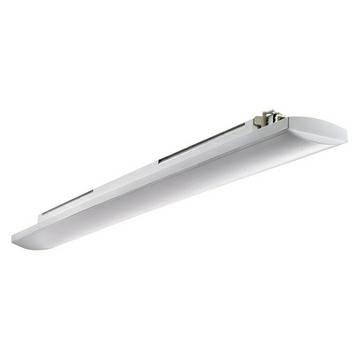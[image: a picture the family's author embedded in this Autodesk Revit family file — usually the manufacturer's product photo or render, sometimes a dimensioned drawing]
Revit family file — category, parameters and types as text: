
# Revit family: Lighting-Industriale-GEWISS-SMART[3]-PLAFONIERA-LED_OPALE_1200mm
name_source: partatom
category: Apparecchi per illuminazione
units: mm (PartAtom-declared; Revit-internal decimal feet)

## family parameters
Condiviso = No
Host = Superficie
Numero OmniClass = 23.80.70.11
Punto di calcolo locali = Sì
Quota connettore circolare = Usa diametro
Sorgente d'illuminazione = No
Taglio con vuoti quando caricato = No
Tipo di parte = Normale
Titolo OmniClass = Luminaries for Internal Lighting

## types (1)
- Lighting-Industriale-GEWISS-SMART[3]-PLAFONIERA-LED_OPALE_1200mm
    Apparecchio a ridotta temperatura superficiale = Conforme
    Applicazione = Interno
    Carico apparente = 45 VA
    Catalogo = LIGHTING
    Catalogo Serie = SMART [3]
    Classe di efficienza LED integrati = A ÷ A++
    Classe isolamento = II
    Codice EAN = 8011564877061
    Codice Electrocod = 2434
    Commenti sul wattaggio = 45W
    Descrizione = SMART3 1200 63LED 45W OPALE DALI 3000K
    Failure rate apparecchio (35.000h, Tq=35° C) = <2,5%
    Failure rate apparecchio (50.000h, Tq=25° C) = <2,5%
    Flusso nominale (lm) = 5500
    Ganci = GEWISS  - ALLUMINIO
    Garanzia = 5 anni
    Glow Wire Test = 850°C
    Grado di protezione = IP66/IP69
    IDF = 88a93abf-ed4e-4284-b5e5-3f2e7fa50ef6
    IDT = 6d1ae202-d28e-42ab-a03c-f890c181dcac
    Immagine tipo = GWS3136P.jpg
    LED Life time (L70) = 80000H
    LED Life time (L80B50) = 100000H
    LED Life time (L90B50) = 50000H
    LED LifeTime (L80B20) = 85000H
    Lampada = LED
    Lampada: = LED
    Lumen output (lm) = 4500
    Lunghezza = 1200 mm
    Lunghezza Lampada = 1200 mm
    Modello = GWS3236PD30K
    N° LED (#) = 63
    Peso (kg): = 2
    Potenza di sistema = 40W
    Produttore = GEWISS S.p.A.
    Prospetto di default = 1219 mm
    Resistenza agli urti = IK08
    SEO = Plafoniera
    Scheda Tecnica = https://www.gewiss.com
    Schermo = Opale
    Schermo. = Gewiss - Led Acceso
    Stampa 1_100 = Sì
    Stampa 1_200 = No
    Struttura = GEWISS - SMART 3 - GRIGIO
    Temperatura di colore = 3000 K (CRI 80)
    Temperatura di colore: = 3000 K (CRI 80)
    Temperatura di funzionamento = -25 +50 °C
    Temperatura di utilizzo = -30 +50 °C
    Tensione = 220/240 V - 50/60 Hz - Dali
    Tipo alimentatore = Driver Led in corrente continua
    Tipologia = DALI
    Tipologia sorgente luminosa = LED - Non sostituibile
    URL = https://www.gewiss.com
    Versione file RFA = 20.11
